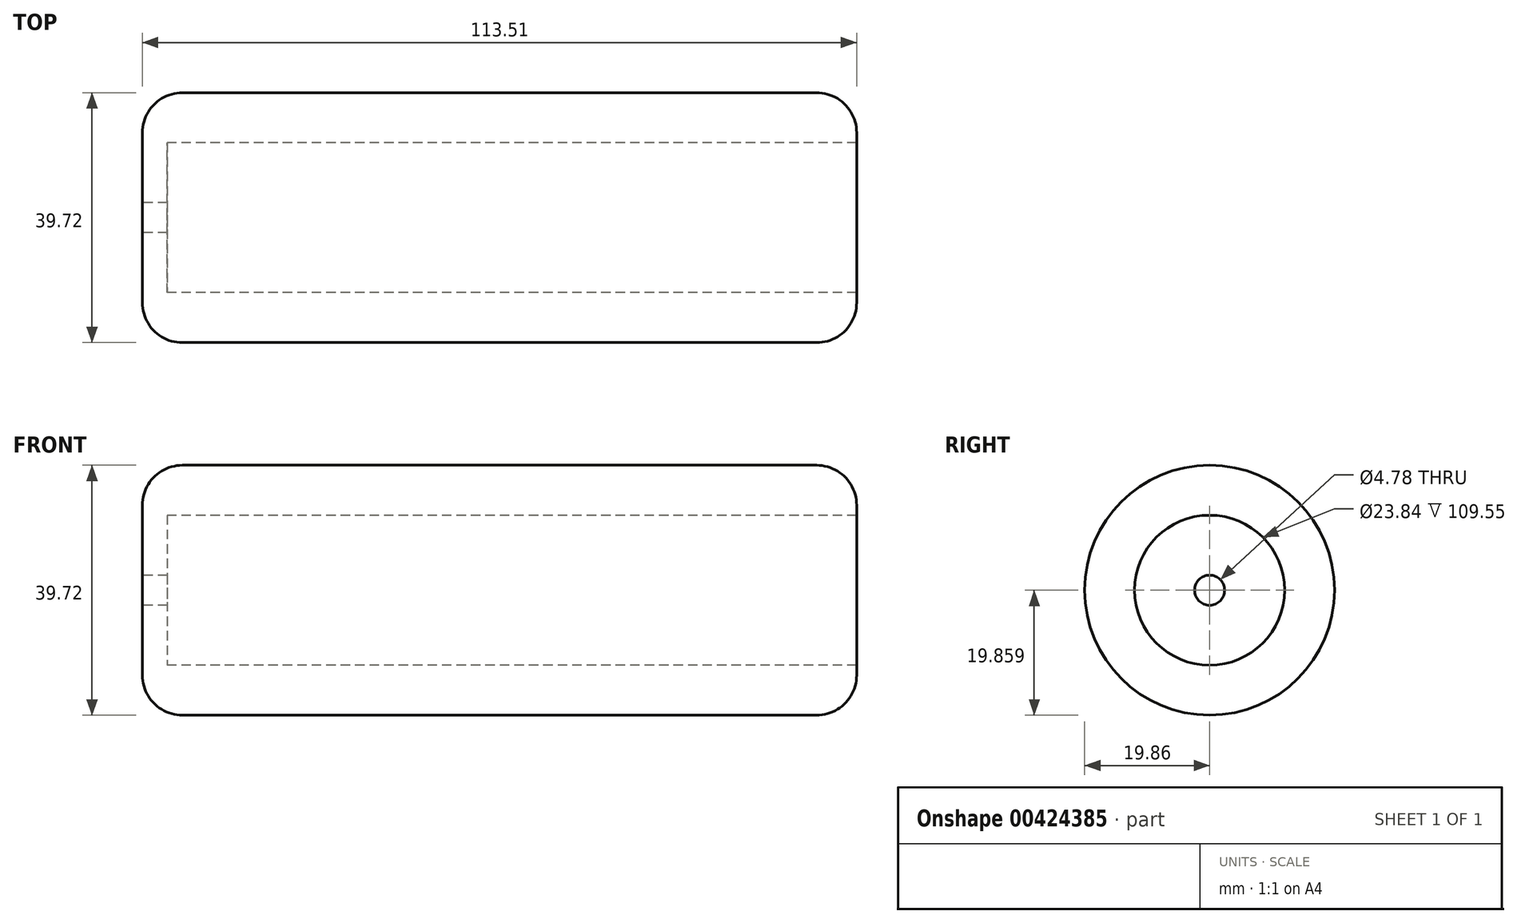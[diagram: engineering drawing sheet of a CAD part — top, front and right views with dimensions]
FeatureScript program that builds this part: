
annotation { "Feature Type Name" : "Feature", "Feature Type Description" : "" }
export const myFeature = defineFeature(function(context is Context, id is Id, definition is map)
    precondition{}
    {
        {
            var Q0;
            Q0=qCreatedBy(makeId("Front.planeOp"),FACE);
            var sketch = newSketch(context, id + "F0", { "sketchPlane" : qUnion([Q0])});
            skLineSegment(sketch, "E0", {"start": v(0, -18.8) * mm, "end": v(3.96, -18.8) * mm});
            skLineSegment(sketch, "E1", {"start": v(3.96, -18.8) * mm, "end": v(3.96, -28.33) * mm});
            skLineSegment(sketch, "E2", {"start": v(3.96, -28.33) * mm, "end": v(113.51, -28.33) * mm});
            skLineSegment(sketch, "E3", {"start": v(113.51, -28.33) * mm, "end": v(113.51, -36.27) * mm});
            skLineSegment(sketch, "E4", {"start": v(113.51, -36.27) * mm, "end": v(0, -36.27) * mm});
            skLineSegment(sketch, "E5", {"start": v(0, -36.27) * mm, "end": v(0, -18.8) * mm});
            skLineSegment(sketch, "E6.0", {"start": v(0, -16.41) * mm, "end": v(3.96, -16.41) * mm, "construction": true});
            skSolve(sketch);
        }
        {
            var Q0;
            Q0=makeQuery(id+"F0.imprint","IMPRINT",FACE,{"disambiguationData":[TD([[makeQuery(id+"F0.imprint","IMPRINT",EDGE,{"derivedFrom":sQuery(id+"F0.wireOp",EDGE,"E0")}),-1.0]])]});
            var Q1;
            Q1=sQuery(id+"F0.wireOp",EDGE,"E6.0");
            revolve(context, id + "F1", {"entities" : qUnion([Q0]), "axis" : qUnion([Q1]), "revolveType" : RevolveType.FULL});
        }
        {
            var Q0;
            Q0=makeQuery(id+"F1.opRevolve","SWEPT_FACE",FACE,{"disambiguationData":[OSD([sQuery(id+"F0.wireOp",EDGE,"E4")])]});
            fillet(context, id + "F2", {"entities" : qUnion([Q0]), "radius" : 6.35 * mm, "tangentPropagation" : true, "allowEdgeOverflow" : false});
        }
    });
